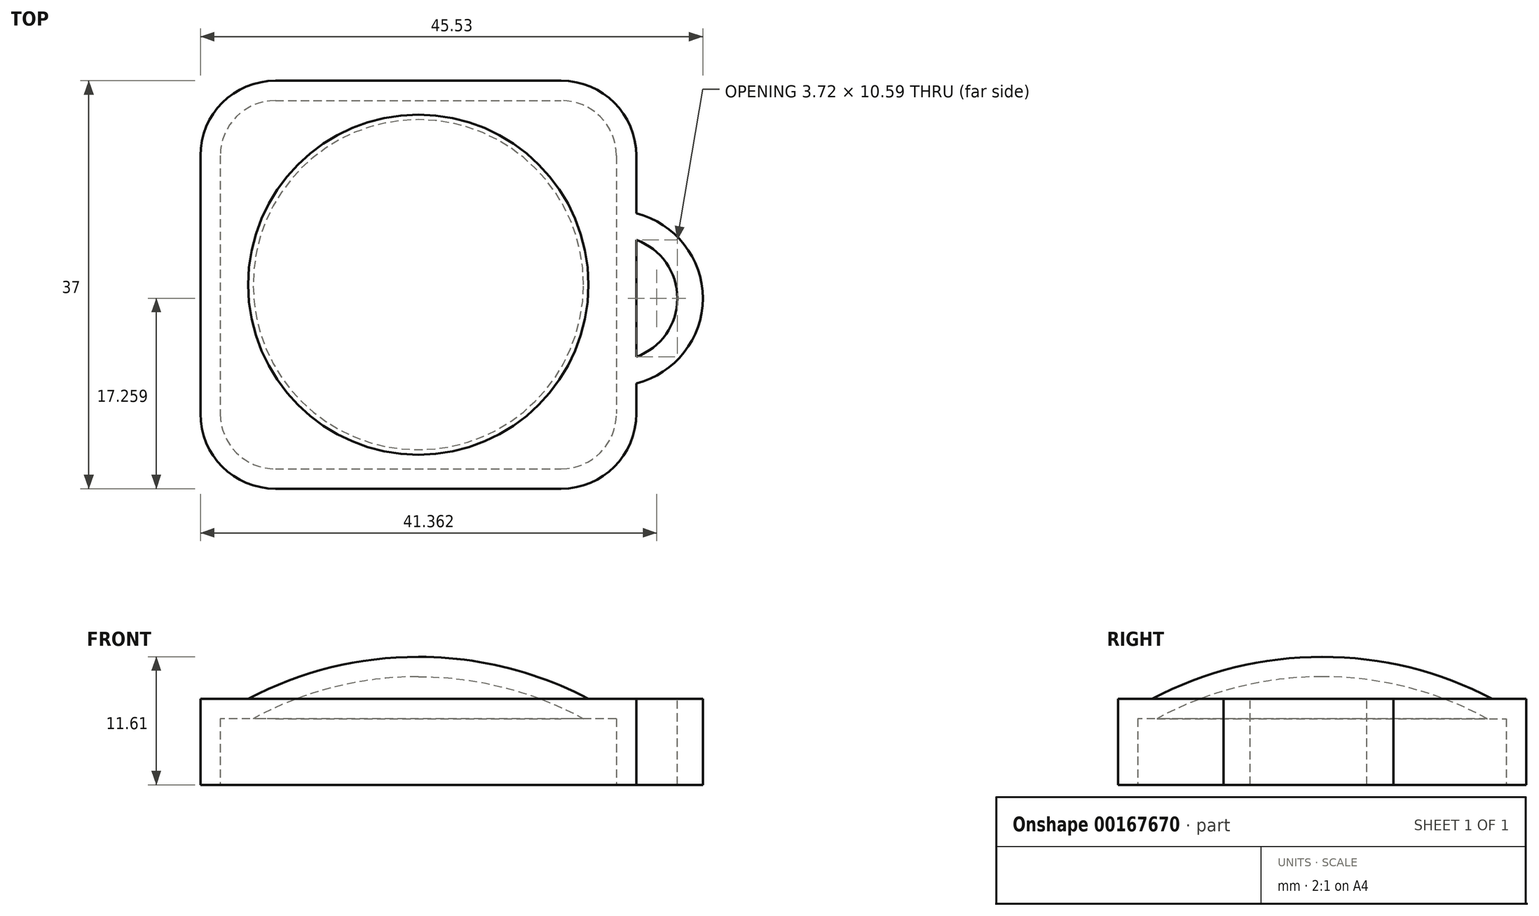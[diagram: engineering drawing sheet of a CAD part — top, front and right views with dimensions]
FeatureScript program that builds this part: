
annotation { "Feature Type Name" : "Feature", "Feature Type Description" : "" }
export const myFeature = defineFeature(function(context is Context, id is Id, definition is map)
    precondition{}
    {
        {
            var Q0;
            Q0=qCreatedBy(makeId("Top.planeOp"),FACE);
            var sketch = newSketch(context, id + "F0", { "sketchPlane" : qUnion([Q0])});
            skLineSegment(sketch, "E0.bottom", {"start": v(-12.95, 16.7) * mm, "end": v(12.95, 16.7) * mm});
            skLineSegment(sketch, "E0.top", {"start": v(-12.95, -16.7) * mm, "end": v(12.95, -16.7) * mm});
            skLineSegment(sketch, "E0.left", {"start": v(-17.95, 11.7) * mm, "end": v(-17.95, -11.7) * mm});
            skLineSegment(sketch, "E0.right", {"start": v(17.95, 11.7) * mm, "end": v(17.95, -11.7) * mm});
            skPoint(sketch, "E1.visualSharp", {"position": v(-17.95, 16.7) * mm});
            skArc(sketch, "E1.filletArc", {"start": v(-12.95, 16.7) * mm, "mid": v(-16.49, 15.24) * mm, "end": v(-17.95, 11.7) * mm});
            skPoint(sketch, "E2.visualSharp", {"position": v(17.95, 16.7) * mm});
            skArc(sketch, "E2.filletArc", {"start": v(17.95, 11.7) * mm, "mid": v(16.49, 15.24) * mm, "end": v(12.95, 16.7) * mm});
            skPoint(sketch, "E3.visualSharp", {"position": v(17.95, -16.7) * mm});
            skArc(sketch, "E3.filletArc", {"start": v(12.95, -16.7) * mm, "mid": v(16.49, -15.24) * mm, "end": v(17.95, -11.7) * mm});
            skPoint(sketch, "E4.visualSharp", {"position": v(-17.95, -16.7) * mm});
            skArc(sketch, "E4.filletArc", {"start": v(-17.95, -11.7) * mm, "mid": v(-16.49, -15.24) * mm, "end": v(-12.95, -16.7) * mm});
            skLineSegment(sketch, "E5", {"start": v(0, -16.7) * mm, "end": v(0, 16.7) * mm, "construction": true});
            skLineSegment(sketch, "E6", {"start": v(-17.95, 0) * mm, "end": v(0, 0) * mm, "construction": true});
            skSolve(sketch);
        }
        {
            var Q0;
            Q0=makeQuery(id+"F0.imprint","IMPRINT",FACE,{"disambiguationData":[TD([[makeQuery(id+"F0.imprint","IMPRINT",EDGE,{"derivedFrom":sQuery(id+"F0.wireOp",EDGE,"E0.bottom")}),-1.0]])]});
            extrude(context, id + "F1", {"entities" : qUnion([Q0]), "depth" : 6 * mm});
        }
        {
            var Q0;
            Q0=qCreatedBy(makeId("Front.planeOp"),FACE);
            var sketch = newSketch(context, id + "F2", { "sketchPlane" : qUnion([Q0])});
            skCircle(sketch, "E7", {"center": v(0, -21.53) * mm, "radius": 31.34 * mm});
            skLineSegment(sketch, "E8.0", {"start": v(-12.95, 6) * mm, "end": v(12.95, 6) * mm});
            skLineSegment(sketch, "E9", {"start": v(0, 6) * mm, "end": v(0, 9.8) * mm});
            skLineSegment(sketch, "E10.0", {"start": v(-17.95, 6) * mm, "end": v(-12.95, 6) * mm});
            skLineSegment(sketch, "E11.0", {"start": v(12.95, 6) * mm, "end": v(17.95, 6) * mm});
            skLineSegment(sketch, "E12", {"start": v(0, 6) * mm, "end": v(0, -52.87) * mm});
            skSolve(sketch);
        }
        {
            var Q0;
            {var subQ0=sQuery(id+"F2.wireOp",EDGE,"E9");Q0=makeQuery(id+"F2.imprint","IMPRINT",FACE,{"disambiguationData":[TD([[makeQuery(id+"F2.imprint","IMPRINT",EDGE,{"derivedFrom":subQ0}),-1.0]])]});}
            var Q1;
            Q1=sQuery(id+"F2.wireOp",EDGE,"E9");
            revolve(context, id + "F3", {"operationType" : NewBodyOperationType.ADD, "entities" : qUnion([Q0]), "axis" : qUnion([Q1]), "revolveType" : RevolveType.FULL});
        }
        {
            var Q0;
            Q0=makeQuery(id+"F1.opExtrude","CAP_FACE",FACE,{"disambiguationData":[OSD([sQuery(id+"F0.wireOp",EDGE,"E0.bottom"),sQuery(id+"F0.wireOp",EDGE,"E0.top"),sQuery(id+"F0.wireOp",EDGE,"E0.left"),sQuery(id+"F0.wireOp",EDGE,"E0.right"),sQuery(id+"F0.wireOp",EDGE,"E1.filletArc"),sQuery(id+"F0.wireOp",EDGE,"E2.filletArc"),sQuery(id+"F0.wireOp",EDGE,"E3.filletArc"),sQuery(id+"F0.wireOp",EDGE,"E4.filletArc")])],"isStart":true});
            shell(context, id + "F4", {"entities" : qUnion([Q0]), "thickness" : 1.8 * mm, "oppositeDirection" : true});
        }
        {
            var Q0;
            Q0=makeQuery(id+"F1.opExtrude","CAP_FACE",FACE,{"disambiguationData":[OSD([sQuery(id+"F0.wireOp",EDGE,"E0.bottom"),sQuery(id+"F0.wireOp",EDGE,"E0.top"),sQuery(id+"F0.wireOp",EDGE,"E0.left"),sQuery(id+"F0.wireOp",EDGE,"E0.right"),sQuery(id+"F0.wireOp",EDGE,"E1.filletArc"),sQuery(id+"F0.wireOp",EDGE,"E2.filletArc"),sQuery(id+"F0.wireOp",EDGE,"E3.filletArc"),sQuery(id+"F0.wireOp",EDGE,"E4.filletArc")])],"isStart":false});
            var sketch = newSketch(context, id + "F5", { "sketchPlane" : qUnion([Q0])});
            skCircle(sketch, "E13", {"center": v(17.85, -1.24) * mm, "radius": 5.63 * mm});
            skCircle(sketch, "E14", {"center": v(17.85, -1.24) * mm, "radius": 7.93 * mm});
            skLineSegment(sketch, "E15.0", {"start": v(19.75, 11.7) * mm, "end": v(19.75, -11.7) * mm});
            skSolve(sketch);
        }
        {
            var Q0;
            {var subQ0=sQuery(id+"F5.wireOp",EDGE,"E15.0");var subQ1=sQuery(id+"F5.wireOp",EDGE,"E13");var subQ2=makeQuery(id+"F5.imprint","INTERSECT",VERTEX,{"disambiguationData":[OD(0.0)],"derivedFrom":[subQ1,subQ0]});Q0=makeQuery(id+"F5.imprint","IMPRINT",FACE,{"disambiguationData":[TD([[makeQuery(id+"F5.imprint","IMPRINT",EDGE,{"disambiguationData":[TD([[subQ2,1.0]])],"derivedFrom":subQ1}),-1.0]])]});}
            var Q1;
            Q1=qCreatedBy(makeId("Top.planeOp"),FACE);
            extrude(context, id + "F6", {"entities" : qUnion([Q0]), "operationType" : NewBodyOperationType.ADD, "endBound" : BoundingType.UP_TO_SURFACE, "oppositeDirection" : true, "endBoundEntityFace" : qUnion([Q1]), "depth" : 25 * mm});
        }
    });
